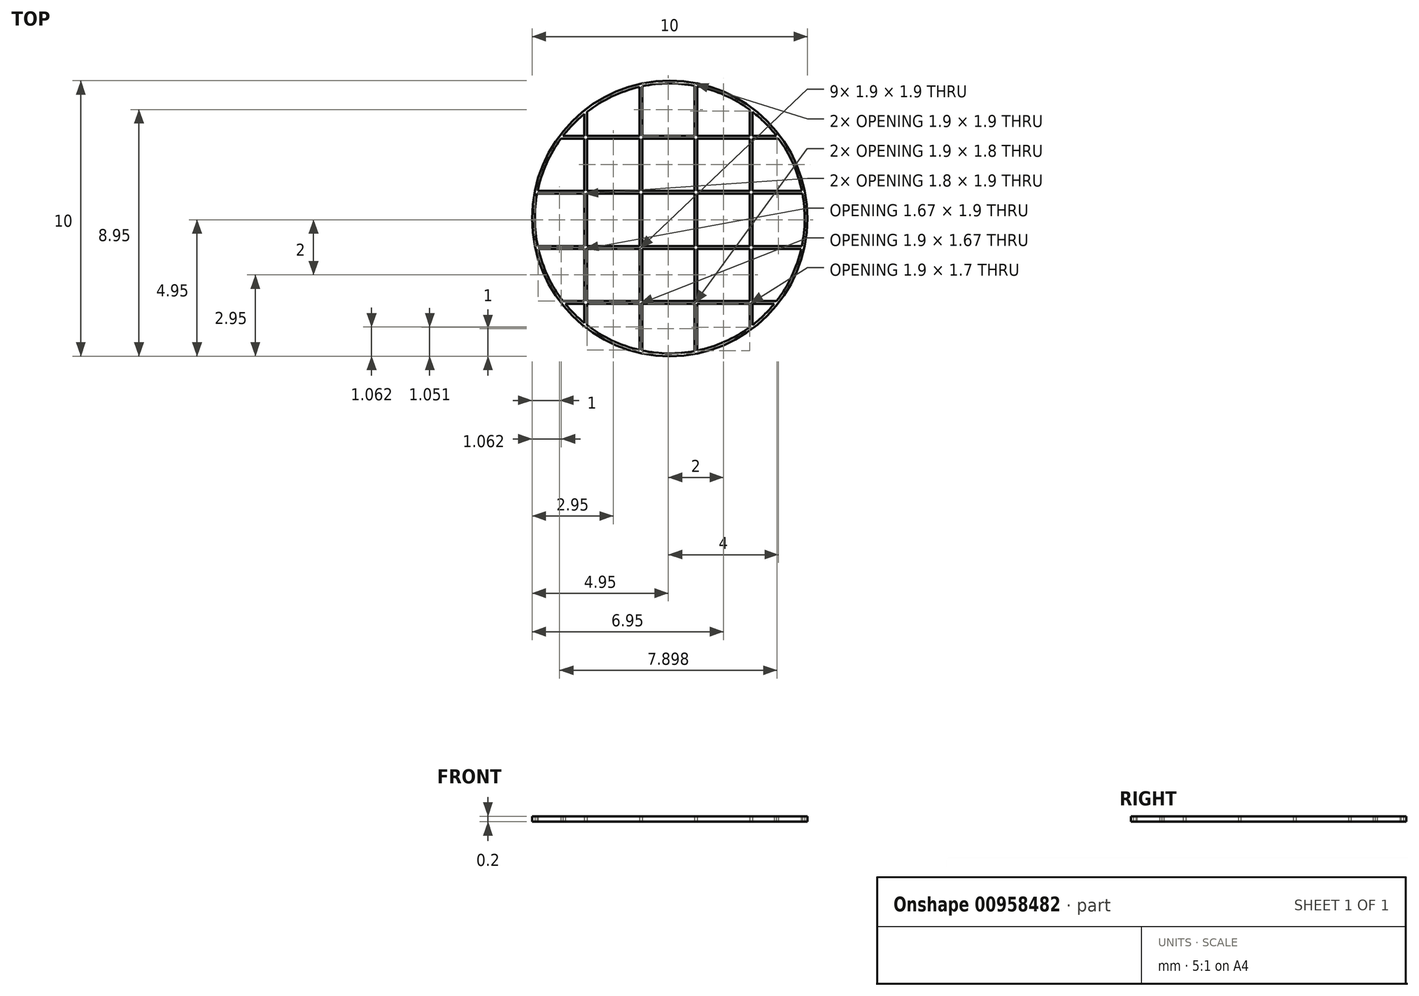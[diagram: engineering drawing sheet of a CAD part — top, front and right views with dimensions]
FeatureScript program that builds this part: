
annotation { "Feature Type Name" : "Feature", "Feature Type Description" : "" }
export const myFeature = defineFeature(function(context is Context, id is Id, definition is map)
    precondition{}
    {
        {
            var Q0;
            Q0=qCreatedBy(makeId("Top.planeOp"),FACE);
            var sketch = newSketch(context, id + "F0", { "sketchPlane" : qUnion([Q0])});
            skCircle(sketch, "E0", {"center": v(0, 0) * mm, "radius": 5 * mm});
            skArc(sketch, "E1", {"start": v(-3.95, 2.9) * mm, "mid": v(-4.48, 2) * mm, "end": v(-4.8, 1) * mm});
            skLineSegment(sketch, "E2.trimOffspring", {"start": v(-3, 3.87) * mm, "end": v(-3, 3) * mm});
            skLineSegment(sketch, "E3.trimOffspring", {"start": v(-3.1, 3.8) * mm, "end": v(-3.1, 3) * mm});
            skLineSegment(sketch, "E4.trimOffspring", {"start": v(-3.1, 3) * mm, "end": v(-3.87, 3) * mm});
            skLineSegment(sketch, "E5.trimOffspring", {"start": v(-3.1, 2.9) * mm, "end": v(-3.95, 2.9) * mm});
            skLineSegment(sketch, "E6.trimOffspring", {"start": v(-3.1, 2.9) * mm, "end": v(-3.1, 1) * mm});
            skLineSegment(sketch, "E7.trimOffspring", {"start": v(-3, 2.9) * mm, "end": v(-3, 1) * mm});
            skArc(sketch, "E8.trimOffspring", {"start": v(-3.1, 3.8) * mm, "mid": v(-3.5, 3.42) * mm, "end": v(-3.87, 3) * mm});
            skLineSegment(sketch, "E9.trimOffspring", {"start": v(-1, 4.8) * mm, "end": v(-1, 3) * mm});
            skLineSegment(sketch, "E10.trimOffspring", {"start": v(-1.1, 4.77) * mm, "end": v(-1.1, 3) * mm});
            skArc(sketch, "E11.trimOffspring", {"start": v(-1.1, 4.77) * mm, "mid": v(-2.1, 4.43) * mm, "end": v(-3, 3.87) * mm});
            skLineSegment(sketch, "E12.trimOffspring", {"start": v(-1.1, 3) * mm, "end": v(-3, 3) * mm});
            skLineSegment(sketch, "E13.trimOffspring", {"start": v(-1, 2.9) * mm, "end": v(-1, 1) * mm});
            skLineSegment(sketch, "E14.trimOffspring", {"start": v(-1.1, 2.9) * mm, "end": v(-3, 2.9) * mm});
            skLineSegment(sketch, "E15.trimOffspring", {"start": v(-1.1, 2.9) * mm, "end": v(-1.1, 1) * mm});
            skLineSegment(sketch, "E16.trimOffspring", {"start": v(0.9, 2.9) * mm, "end": v(0.9, 1) * mm});
            skLineSegment(sketch, "E17.trimOffspring", {"start": v(0.9, 3) * mm, "end": v(-1, 3) * mm});
            skLineSegment(sketch, "E18.trimOffspring", {"start": v(1, 2.9) * mm, "end": v(1, 1) * mm});
            skLineSegment(sketch, "E19.trimOffspring", {"start": v(0.9, 2.9) * mm, "end": v(-1, 2.9) * mm});
            skLineSegment(sketch, "E20.trimOffspring", {"start": v(0.9, 4.82) * mm, "end": v(0.9, 3) * mm});
            skArc(sketch, "E21.trimOffspring", {"start": v(0.9, 4.82) * mm, "mid": v(-0.05, 4.9) * mm, "end": v(-1, 4.8) * mm});
            skLineSegment(sketch, "E22.trimOffspring", {"start": v(1, 4.8) * mm, "end": v(1, 3) * mm});
            skLineSegment(sketch, "E23.trimOffspring", {"start": v(2.9, 3.95) * mm, "end": v(2.9, 3) * mm});
            skLineSegment(sketch, "E24.trimOffspring", {"start": v(3, 3.87) * mm, "end": v(3, 3) * mm});
            skArc(sketch, "E25.trimOffspring", {"start": v(2.9, 3.95) * mm, "mid": v(2, 4.48) * mm, "end": v(1, 4.8) * mm});
            skLineSegment(sketch, "E26.trimOffspring", {"start": v(2.9, 3) * mm, "end": v(1, 3) * mm});
            skLineSegment(sketch, "E27.trimOffspring", {"start": v(2.9, 2.9) * mm, "end": v(2.9, 1) * mm});
            skLineSegment(sketch, "E28.trimOffspring", {"start": v(2.9, 2.9) * mm, "end": v(1, 2.9) * mm});
            skLineSegment(sketch, "E29.trimOffspring", {"start": v(3, 2.9) * mm, "end": v(3, 1) * mm});
            skLineSegment(sketch, "E30.trimOffspring", {"start": v(3.87, 3) * mm, "end": v(3, 3) * mm});
            skArc(sketch, "E31.trimOffspring", {"start": v(3.87, 3) * mm, "mid": v(3.46, 3.46) * mm, "end": v(3, 3.87) * mm});
            skLineSegment(sketch, "E32.trimOffspring", {"start": v(3.95, 2.9) * mm, "end": v(3, 2.9) * mm});
            skLineSegment(sketch, "E33.trimOffspring", {"start": v(4.8, 1) * mm, "end": v(3, 1) * mm});
            skLineSegment(sketch, "E34.trimOffspring", {"start": v(4.82, 0.9) * mm, "end": v(3, 0.9) * mm});
            skArc(sketch, "E35.trimOffspring", {"start": v(4.8, 1) * mm, "mid": v(4.48, 2) * mm, "end": v(3.95, 2.9) * mm});
            skLineSegment(sketch, "E36.trimOffspring", {"start": v(2.9, 1) * mm, "end": v(1, 1) * mm});
            skLineSegment(sketch, "E37.trimOffspring", {"start": v(2.9, 0.9) * mm, "end": v(2.9, -1) * mm});
            skLineSegment(sketch, "E38.trimOffspring", {"start": v(3, 0.9) * mm, "end": v(3, -1) * mm});
            skLineSegment(sketch, "E39.trimOffspring", {"start": v(2.9, 0.9) * mm, "end": v(1, 0.9) * mm});
            skLineSegment(sketch, "E40.trimOffspring", {"start": v(0.9, 1) * mm, "end": v(-1, 1) * mm});
            skLineSegment(sketch, "E41.trimOffspring", {"start": v(1, 0.9) * mm, "end": v(1, -1) * mm});
            skLineSegment(sketch, "E42.trimOffspring", {"start": v(0.9, 0.9) * mm, "end": v(-1, 0.9) * mm});
            skLineSegment(sketch, "E43.trimOffspring", {"start": v(0.9, 0.9) * mm, "end": v(0.9, -1) * mm});
            skLineSegment(sketch, "E44.trimOffspring", {"start": v(-1.1, 1) * mm, "end": v(-3, 1) * mm});
            skLineSegment(sketch, "E45.trimOffspring", {"start": v(-1, 0.9) * mm, "end": v(-1, -1) * mm});
            skLineSegment(sketch, "E46.trimOffspring", {"start": v(-1.1, 0.9) * mm, "end": v(-3, 0.9) * mm});
            skLineSegment(sketch, "E47.trimOffspring", {"start": v(-1.1, 0.9) * mm, "end": v(-1.1, -1) * mm});
            skLineSegment(sketch, "E48.trimOffspring", {"start": v(-3.1, 1) * mm, "end": v(-4.8, 1) * mm});
            skLineSegment(sketch, "E49.trimOffspring", {"start": v(-3, 0.9) * mm, "end": v(-3, -1) * mm});
            skLineSegment(sketch, "E50.trimOffspring", {"start": v(-3.1, 0.9) * mm, "end": v(-4.82, 0.9) * mm});
            skLineSegment(sketch, "E51.trimOffspring", {"start": v(-3.1, 0.9) * mm, "end": v(-3.1, -1) * mm});
            skArc(sketch, "E52.trimOffspring", {"start": v(-4.82, 0.9) * mm, "mid": v(-4.9, -0.05) * mm, "end": v(-4.8, -1) * mm});
            skArc(sketch, "E53.trimOffspring", {"start": v(-4.77, -1.1) * mm, "mid": v(-4.43, -2.1) * mm, "end": v(-3.87, -3) * mm});
            skLineSegment(sketch, "E54.trimOffspring", {"start": v(-3.1, -1.1) * mm, "end": v(-3.1, -3) * mm});
            skLineSegment(sketch, "E55.trimOffspring", {"start": v(-3.1, -1) * mm, "end": v(-4.8, -1) * mm});
            skLineSegment(sketch, "E56.trimOffspring", {"start": v(-3, -1.1) * mm, "end": v(-3, -3) * mm});
            skLineSegment(sketch, "E57.trimOffspring", {"start": v(-3.1, -1.1) * mm, "end": v(-4.77, -1.1) * mm});
            skLineSegment(sketch, "E58.trimOffspring", {"start": v(-1.1, -1) * mm, "end": v(-3, -1) * mm});
            skLineSegment(sketch, "E59.trimOffspring", {"start": v(-1.1, -1.1) * mm, "end": v(-1.1, -3) * mm});
            skLineSegment(sketch, "E60.trimOffspring", {"start": v(-1.1, -1.1) * mm, "end": v(-3, -1.1) * mm});
            skLineSegment(sketch, "E61.trimOffspring", {"start": v(-1, -1.1) * mm, "end": v(-1, -3) * mm});
            skLineSegment(sketch, "E62.trimOffspring", {"start": v(0.9, -1) * mm, "end": v(-1, -1) * mm});
            skLineSegment(sketch, "E63.trimOffspring", {"start": v(0.9, -1.1) * mm, "end": v(0.9, -3) * mm});
            skLineSegment(sketch, "E64.trimOffspring", {"start": v(0.9, -1.1) * mm, "end": v(-1, -1.1) * mm});
            skLineSegment(sketch, "E65.trimOffspring", {"start": v(1, -1.1) * mm, "end": v(1, -3) * mm});
            skLineSegment(sketch, "E66.trimOffspring", {"start": v(2.9, -1) * mm, "end": v(1, -1) * mm});
            skLineSegment(sketch, "E67.trimOffspring", {"start": v(2.9, -1.1) * mm, "end": v(2.9, -3) * mm});
            skLineSegment(sketch, "E68.trimOffspring", {"start": v(2.9, -1.1) * mm, "end": v(1, -1.1) * mm});
            skLineSegment(sketch, "E69.trimOffspring", {"start": v(3, -1.1) * mm, "end": v(3, -3) * mm});
            skLineSegment(sketch, "E70.trimOffspring", {"start": v(4.8, -1) * mm, "end": v(3, -1) * mm});
            skArc(sketch, "E71.trimOffspring", {"start": v(4.8, -1) * mm, "mid": v(4.9, -0.05) * mm, "end": v(4.82, 0.9) * mm});
            skLineSegment(sketch, "E72.trimOffspring", {"start": v(4.77, -1.1) * mm, "end": v(3, -1.1) * mm});
            skLineSegment(sketch, "E73.trimOffspring", {"start": v(3.87, -3) * mm, "end": v(3, -3) * mm});
            skArc(sketch, "E74.trimOffspring", {"start": v(3.87, -3) * mm, "mid": v(4.43, -2.1) * mm, "end": v(4.77, -1.1) * mm});
            skLineSegment(sketch, "E75.trimOffspring", {"start": v(3.8, -3.1) * mm, "end": v(3, -3.1) * mm});
            skLineSegment(sketch, "E76.trimOffspring", {"start": v(3, -3.1) * mm, "end": v(3, -3.87) * mm});
            skLineSegment(sketch, "E77.trimOffspring", {"start": v(2.9, -3) * mm, "end": v(1, -3) * mm});
            skLineSegment(sketch, "E78.trimOffspring", {"start": v(2.9, -3.1) * mm, "end": v(2.9, -3.95) * mm});
            skLineSegment(sketch, "E79.trimOffspring", {"start": v(2.9, -3.1) * mm, "end": v(1, -3.1) * mm});
            skLineSegment(sketch, "E80.trimOffspring", {"start": v(0.9, -3) * mm, "end": v(-1, -3) * mm});
            skLineSegment(sketch, "E81.trimOffspring", {"start": v(0.9, -3.1) * mm, "end": v(-1, -3.1) * mm});
            skLineSegment(sketch, "E82.trimOffspring", {"start": v(0.9, -3.1) * mm, "end": v(0.9, -4.82) * mm});
            skLineSegment(sketch, "E83.trimOffspring", {"start": v(1, -3.1) * mm, "end": v(1, -4.8) * mm});
            skLineSegment(sketch, "E84.trimOffspring", {"start": v(-1.1, -3) * mm, "end": v(-3, -3) * mm});
            skLineSegment(sketch, "E85.trimOffspring", {"start": v(-1.1, -3.1) * mm, "end": v(-3, -3.1) * mm});
            skLineSegment(sketch, "E86.trimOffspring", {"start": v(-1.1, -3.1) * mm, "end": v(-1.1, -4.77) * mm});
            skLineSegment(sketch, "E87.trimOffspring", {"start": v(-1, -3.1) * mm, "end": v(-1, -4.8) * mm});
            skArc(sketch, "E88.trimOffspring", {"start": v(-3.8, -3.1) * mm, "mid": v(-3.46, -3.46) * mm, "end": v(-3.1, -3.8) * mm});
            skLineSegment(sketch, "E89.trimOffspring", {"start": v(-3.1, -3.1) * mm, "end": v(-3.1, -3.8) * mm});
            skLineSegment(sketch, "E90.trimOffspring", {"start": v(-3.1, -3) * mm, "end": v(-3.87, -3) * mm});
            skLineSegment(sketch, "E91.trimOffspring", {"start": v(-3, -3.1) * mm, "end": v(-3, -3.87) * mm});
            skLineSegment(sketch, "E92.trimOffspring", {"start": v(-3.1, -3.1) * mm, "end": v(-3.8, -3.1) * mm});
            skArc(sketch, "E93.trimOffspring", {"start": v(-3, -3.87) * mm, "mid": v(-2.1, -4.43) * mm, "end": v(-1.1, -4.77) * mm});
            skArc(sketch, "E94.trimOffspring", {"start": v(-1, -4.8) * mm, "mid": v(-0.05, -4.9) * mm, "end": v(0.9, -4.82) * mm});
            skArc(sketch, "E95.trimOffspring", {"start": v(1, -4.8) * mm, "mid": v(2, -4.48) * mm, "end": v(2.9, -3.95) * mm});
            skArc(sketch, "E96.trimOffspring", {"start": v(3, -3.87) * mm, "mid": v(3.42, -3.5) * mm, "end": v(3.8, -3.1) * mm});
            skSolve(sketch);
        }
        {
            var Q0;
            Q0=makeQuery(id+"F0.imprint","IMPRINT",FACE,{"disambiguationData":[TD([[makeQuery(id+"F0.imprint","IMPRINT",EDGE,{"derivedFrom":sQuery(id+"F0.wireOp",EDGE,"E0")}),1.0]])]});
            extrude(context, id + "F1", {"entities" : qUnion([Q0]), "depth" : .2 * mm, "offsetDistance" : 25 * mm});
        }
    });
